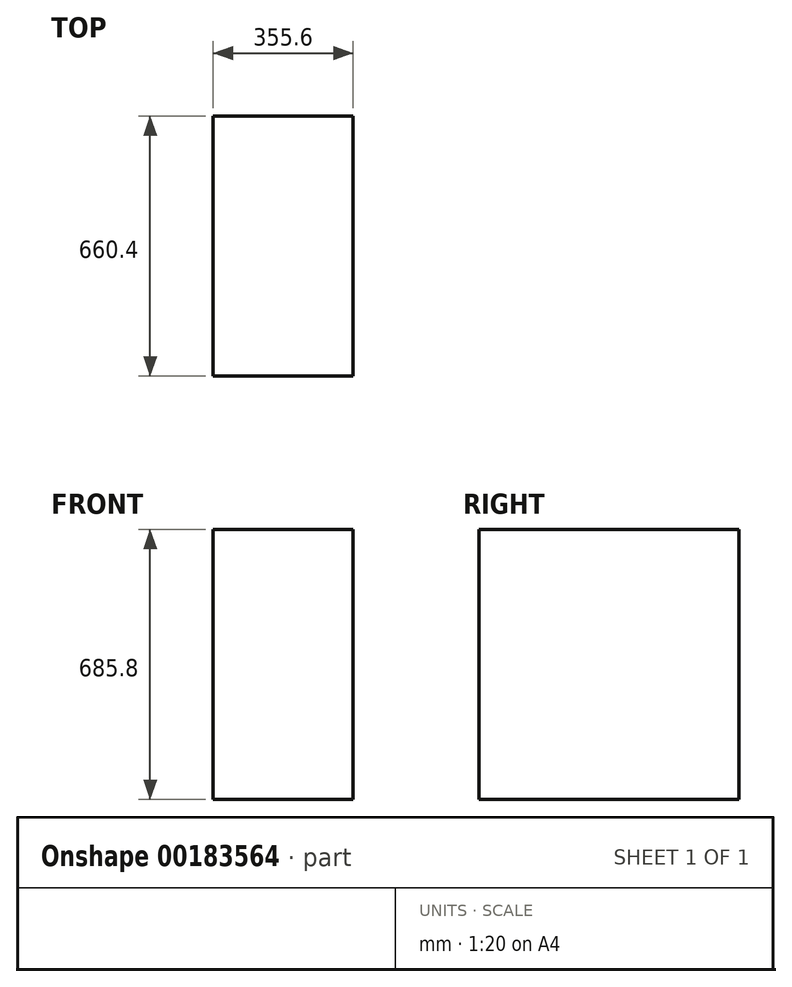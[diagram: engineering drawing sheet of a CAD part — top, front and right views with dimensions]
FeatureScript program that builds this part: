
annotation { "Feature Type Name" : "Feature", "Feature Type Description" : "" }
export const myFeature = defineFeature(function(context is Context, id is Id, definition is map)
    precondition{}
    {
        {
            var Q0;
            Q0=qCreatedBy(makeId("Right.planeOp"),FACE);
            var sketch = newSketch(context, id + "F0", { "sketchPlane" : qUnion([Q0])});
            skLineSegment(sketch, "E0.bottom", {"start": v(-330.2, 342.9) * mm, "end": v(330.2, 342.9) * mm});
            skLineSegment(sketch, "E0.top", {"start": v(-330.2, -342.9) * mm, "end": v(330.2, -342.9) * mm});
            skLineSegment(sketch, "E0.left", {"start": v(-330.2, 342.9) * mm, "end": v(-330.2, -342.9) * mm});
            skLineSegment(sketch, "E0.right", {"start": v(330.2, 342.9) * mm, "end": v(330.2, -342.9) * mm});
            skPoint(sketch, "E0.middle", {"position": v(0, 0) * mm});
            skSolve(sketch);
        }
        {
            var Q0;
            Q0 = qSketchRegion(id + "F0", true);
            extrude(context, id + "F1", {"entities" : qUnion([Q0]), "depth" : 355.6 * mm});
        }
    });
